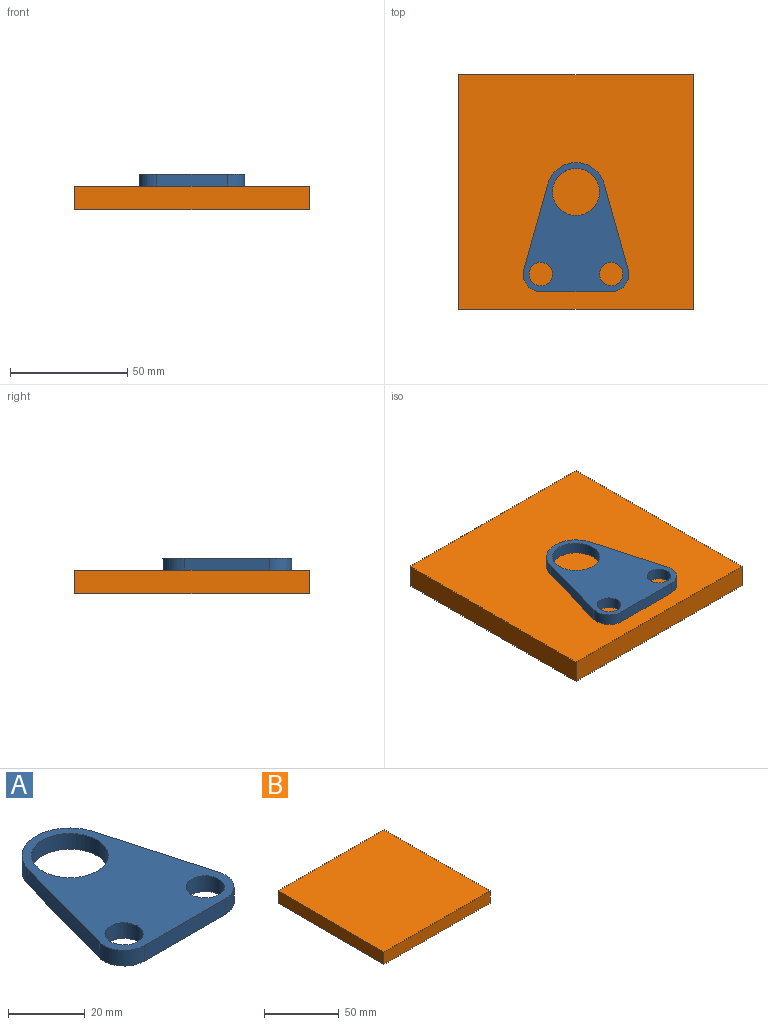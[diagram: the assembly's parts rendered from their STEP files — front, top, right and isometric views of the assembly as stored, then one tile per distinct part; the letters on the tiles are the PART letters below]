
ASSEMBLY  parts=2 mates=1
PART A: 11 faces, bbox 45x55x5 mm
  f0: plane 36.35x10.19mm, normal (0.96,0.27,0), area 188.7mm2, adj f1,f8,f9,f10
  f1: cylinder r=12.5mm len=24.07mm, axis (0,0,-1), area 162.2mm2, adj f0,f2,f9,f10
  f2: plane 36.35x10.19mm, normal (-0.96,0.27,0), area 188.7mm2, adj f1,f3,f9,f10
  f3: cylinder r=7.5mm len=9.52mm, axis (0,0,-1), area 69.2mm2, adj f2,f4,f9,f10
  f4: plane 30x5mm, normal (0,-1,0), area 150mm2, adj f3,f8,f9,f10
  f5: cylinder r=10mm len=20mm, axis (0,0,-1), area 314.2mm2, adj f9,f10
  f6: cylinder r=5mm len=10mm, axis (0,0,-1), area 157.1mm2, adj f9,f10
  f7: cylinder r=5mm len=10mm, axis (0,0,-1), area 157.1mm2, adj f9,f10
  f8: cylinder r=7.5mm len=9.52mm, axis (0,0,-1), area 69.2mm2, adj f0,f4,f9,f10
  f9: plane 55x45mm, normal (0,0,1), area 1340.2mm2, adj f0,f1,f2,f3,f4,f5,f6,f7
  f10: plane 55x45mm, normal (0,0,-1), area 1340.2mm2, adj f0,f1,f2,f3,f4,f5,f6,f7
PART B: 6 faces, bbox 100x100x10 mm
  f0: plane 100x10mm, normal (1,0,0), area 1000mm2, adj f1,f3,f4,f5
  f1: plane 100x10mm, normal (0,1,0), area 1000mm2, adj f0,f2,f4,f5
  f2: plane 100x10mm, normal (-1,0,0), area 1000mm2, adj f1,f3,f4,f5
  f3: plane 100x10mm, normal (0,-1,0), area 1000mm2, adj f0,f2,f4,f5
  f4: plane 100x100mm, normal (0,0,-1), area 10000mm2, adj f0,f1,f2,f3
  f5: plane 100x100mm, normal (0,0,1), area 10000mm2, adj f0,f1,f2,f3
PLACE A at identity
PLACE B at identity
MATE parallel B.f5 <-> A.f1  axis (0,0,1) through (0,0,0)mm
